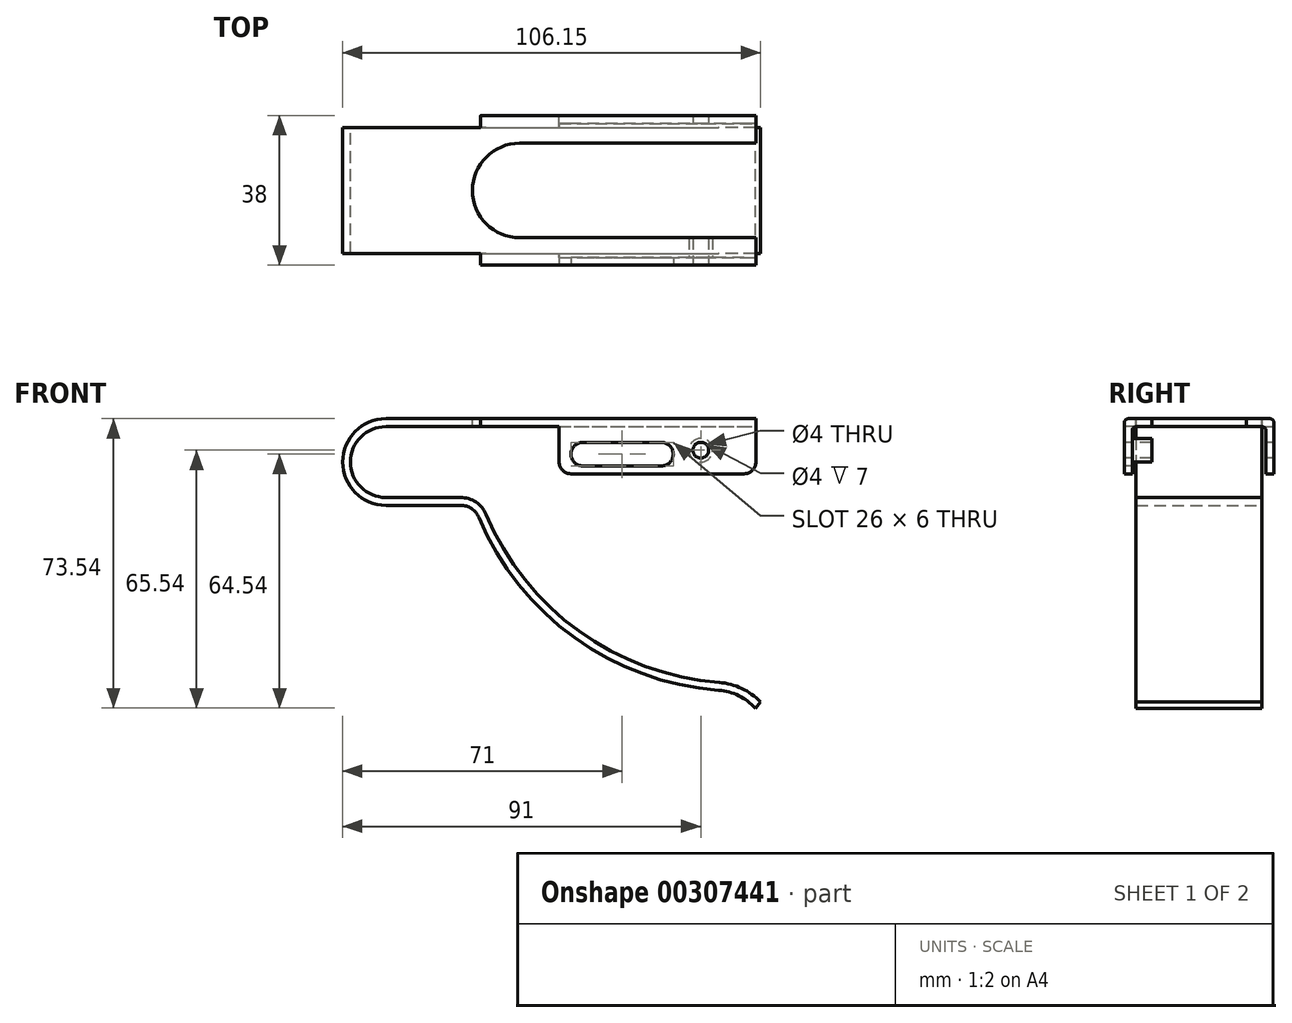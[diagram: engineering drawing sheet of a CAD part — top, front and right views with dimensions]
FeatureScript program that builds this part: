
annotation { "Feature Type Name" : "Feature", "Feature Type Description" : "" }
export const myFeature = defineFeature(function(context is Context, id is Id, definition is map)
    precondition{}
    {
        {
            var Q0;
            Q0=qCreatedBy(makeId("Front.planeOp"),FACE);
            var sketch = newSketch(context, id + "F0", { "sketchPlane" : qUnion([Q0])});
            skArc(sketch, "E0", {"start": v(0, 11) * mm, "mid": v(-11, 0) * mm, "end": v(0, -11) * mm});
            skLineSegment(sketch, "E1", {"start": v(0, 11) * mm, "end": v(94, 11) * mm});
            skLineSegment(sketch, "E2", {"start": v(0, -11) * mm, "end": v(19, -11) * mm});
            skArc(sketch, "E3", {"start": v(23.61, -14.06) * mm, "mid": v(47.9, -44.6) * mm, "end": v(84.55, -58) * mm});
            skArc(sketch, "E4", {"start": v(93.86, -62.54) * mm, "mid": v(89.64, -59.38) * mm, "end": v(84.55, -58) * mm});
            skPoint(sketch, "E5.visualSharp", {"position": v(22.4, -11) * mm});
            skArc(sketch, "E5.filletArc", {"start": v(23.61, -14.06) * mm, "mid": v(21.77, -11.84) * mm, "end": v(19, -11) * mm});
            skLineSegment(sketch, "E6.0", {"start": v(0, 9) * mm, "end": v(94, 9) * mm});
            skArc(sketch, "E6.1", {"start": v(0, 9) * mm, "mid": v(-9, 0) * mm, "end": v(0, -9) * mm});
            skArc(sketch, "E6.2", {"start": v(95.15, -61) * mm, "mid": v(90.4, -57.52) * mm, "end": v(84.7, -56) * mm});
            skArc(sketch, "E6.3", {"start": v(25.45, -13.3) * mm, "mid": v(49.07, -42.99) * mm, "end": v(84.7, -56) * mm});
            skArc(sketch, "E6.4", {"start": v(25.45, -13.3) * mm, "mid": v(22.88, -10.17) * mm, "end": v(19, -9) * mm});
            skLineSegment(sketch, "E6.5", {"start": v(0, -9) * mm, "end": v(19, -9) * mm});
            skLineSegment(sketch, "E7", {"start": v(94, 11) * mm, "end": v(94, 9) * mm});
            skLineSegment(sketch, "E8", {"start": v(95.15, -61) * mm, "end": v(93.86, -62.54) * mm});
            skLineSegment(sketch, "E9", {"start": v(107.63, -61.05) * mm, "end": v(113.07, -61.05) * mm});
            skSolve(sketch);
        }
        {
            var Q0;
            Q0 = qSketchRegion(id + "F0", true);
            extrude(context, id + "F1", {"entities" : qUnion([Q0]), "depth" : 16 * mm});
        }
        {
            var Q0;
            Q0=makeQuery(id+"F1.opExtrude","SWEPT_FACE",FACE,{"disambiguationData":[OSD([sQuery(id+"F0.wireOp",EDGE,"E1")])]});
            var sketch = newSketch(context, id + "F2", { "sketchPlane" : qUnion([Q0])});
            skLineSegment(sketch, "E10.bottom", {"start": v(94, -16) * mm, "end": v(24, -16) * mm});
            skLineSegment(sketch, "E10.top", {"start": v(94, -19) * mm, "end": v(24, -19) * mm});
            skLineSegment(sketch, "E10.left", {"start": v(94, -16) * mm, "end": v(94, -19) * mm});
            skLineSegment(sketch, "E10.right", {"start": v(24, -16) * mm, "end": v(24, -19) * mm});
            skSolve(sketch);
        }
        {
            var Q0;
            Q0 = qSketchRegion(id + "F2", true);
            extrude(context, id + "F3", {"entities" : qUnion([Q0]), "operationType" : NewBodyOperationType.ADD, "oppositeDirection" : true, "depth" : 2 * mm});
        }
        {
            var Q0;
            Q0=makeQuery(id+"F3.opExtrude","SWEPT_FACE",FACE,{"disambiguationData":[OSD([sQuery(id+"F2.wireOp",EDGE,"E10.top")])]});
            var sketch = newSketch(context, id + "F4", { "sketchPlane" : qUnion([Q0])});
            skLineSegment(sketch, "E11.bottom", {"start": v(94, 11) * mm, "end": v(44, 11) * mm});
            skLineSegment(sketch, "E11.top", {"start": v(94, -3) * mm, "end": v(44, -3) * mm});
            skLineSegment(sketch, "E11.left", {"start": v(94, 11) * mm, "end": v(94, -3) * mm});
            skLineSegment(sketch, "E11.right", {"start": v(44, 11) * mm, "end": v(44, -3) * mm});
            skSolve(sketch);
        }
        {
            var Q0;
            Q0 = qSketchRegion(id + "F4", true);
            extrude(context, id + "F5", {"entities" : qUnion([Q0]), "operationType" : NewBodyOperationType.ADD, "oppositeDirection" : true, "depth" : 2 * mm});
        }
        {
            var Q0;
            Q0=makeQuery(id+"F3.opExtrude","CAP_EDGE",EDGE,{"disambiguationData":[OSD([sQuery(id+"F2.wireOp",EDGE,"E10.top")])],"isStart":true});
            var Q1;
            Q1=makeQuery(id+"F5.boolean.opBoolean","INTERSECT",EDGE,{"derivedFrom":[makeQuery(id+"F3.boolean.opBoolean","MERGE",FACE,{"derivedFrom":[makeQuery(id+"F1.opExtrude","SWEPT_FACE",FACE,{"disambiguationData":[OSD([sQuery(id+"F0.wireOp",EDGE,"E6.0")])]}),makeQuery(id+"F3.opExtrude","CAP_FACE",FACE,{"disambiguationData":[OSD([sQuery(id+"F2.wireOp",EDGE,"E10.bottom"),sQuery(id+"F2.wireOp",EDGE,"E10.top"),sQuery(id+"F2.wireOp",EDGE,"E10.left"),sQuery(id+"F2.wireOp",EDGE,"E10.right")])],"isStart":false})]}),makeQuery(id+"F5.opExtrude","CAP_FACE",FACE,{"disambiguationData":[OSD([sQuery(id+"F4.wireOp",EDGE,"E11.bottom"),sQuery(id+"F4.wireOp",EDGE,"E11.top"),sQuery(id+"F4.wireOp",EDGE,"E11.left"),sQuery(id+"F4.wireOp",EDGE,"E11.right")])],"isStart":false})]});
            fillet(context, id + "F6", {"entities" : qUnion([Q0, Q1]), "radius" : 1 * mm, "tangentPropagation" : true, "allowEdgeOverflow" : false});
        }
        {
            var Q0;
            Q0=makeQuery(id+"F1.opExtrude","SWEPT_BODY",BODY,{"disambiguationData":[OSD([sQuery(id+"F0.wireOp",EDGE,"E0"),sQuery(id+"F0.wireOp",EDGE,"E1"),sQuery(id+"F0.wireOp",EDGE,"E2"),sQuery(id+"F0.wireOp",EDGE,"E3"),sQuery(id+"F0.wireOp",EDGE,"E4"),sQuery(id+"F0.wireOp",EDGE,"E5.filletArc"),sQuery(id+"F0.wireOp",EDGE,"E6.0"),sQuery(id+"F0.wireOp",EDGE,"E6.1"),sQuery(id+"F0.wireOp",EDGE,"E6.2"),sQuery(id+"F0.wireOp",EDGE,"E6.3"),sQuery(id+"F0.wireOp",EDGE,"E6.4"),sQuery(id+"F0.wireOp",EDGE,"E6.5"),sQuery(id+"F0.wireOp",EDGE,"E7"),sQuery(id+"F0.wireOp",EDGE,"E8")])]});
            var Q1;
            Q1=qCreatedBy(makeId("Front.planeOp"),FACE);
            mirror(context, id + "F7", {"operationType" : NewBodyOperationType.ADD, "entities" : qUnion([Q0]), "mirrorPlane" : qUnion([Q1])});
        }
        {
            var Q0;
            {var subQ0=makeQuery(id+"F3.boolean.opBoolean","MERGE",FACE,{"derivedFrom":[makeQuery(id+"F1.opExtrude","SWEPT_FACE",FACE,{"disambiguationData":[OSD([sQuery(id+"F0.wireOp",EDGE,"E1")])]}),makeQuery(id+"F3.opExtrude","CAP_FACE",FACE,{"disambiguationData":[OSD([sQuery(id+"F2.wireOp",EDGE,"E10.bottom"),sQuery(id+"F2.wireOp",EDGE,"E10.top"),sQuery(id+"F2.wireOp",EDGE,"E10.left"),sQuery(id+"F2.wireOp",EDGE,"E10.right")])],"isStart":true})]});Q0=makeQuery(id+"F7.boolean.opBoolean","MERGE",FACE,{"derivedFrom":[subQ0,makeQuery(id+"F7.opPattern","COPY",FACE,{"derivedFrom":subQ0,"instanceName":"1"})]});}
            var sketch = newSketch(context, id + "F8", { "sketchPlane" : qUnion([Q0])});
            skArc(sketch, "E12", {"start": v(34, 12) * mm, "mid": v(22, 0) * mm, "end": v(34, -12) * mm});
            skLineSegment(sketch, "E13", {"start": v(34, -12) * mm, "end": v(94, -12) * mm});
            skLineSegment(sketch, "E14", {"start": v(34, 12) * mm, "end": v(94, 12) * mm});
            skSolve(sketch);
        }
        {
            var Q0;
            Q0=makeQuery(id+"F8.imprint","IMPRINT",FACE,{"disambiguationData":[TD([[makeQuery(id+"F8.imprint","IMPRINT",EDGE,{"derivedFrom":sQuery(id+"F8.wireOp",EDGE,"E12")}),1.0]])]});
            extrude(context, id + "F9", {"entities" : qUnion([Q0]), "operationType" : NewBodyOperationType.REMOVE, "oppositeDirection" : true, "depth" : 2 * mm});
        }
        {
            var Q0;
            Q0=makeQuery(id+"F5.boolean.opBoolean","MERGE",FACE,{"derivedFrom":[makeQuery(id+"F3.opExtrude","SWEPT_FACE",FACE,{"disambiguationData":[OSD([sQuery(id+"F2.wireOp",EDGE,"E10.top")])]}),makeQuery(id+"F5.opExtrude","CAP_FACE",FACE,{"disambiguationData":[OSD([sQuery(id+"F4.wireOp",EDGE,"E11.bottom"),sQuery(id+"F4.wireOp",EDGE,"E11.top"),sQuery(id+"F4.wireOp",EDGE,"E11.left"),sQuery(id+"F4.wireOp",EDGE,"E11.right")])],"isStart":true})]});
            var sketch = newSketch(context, id + "F10", { "sketchPlane" : qUnion([Q0])});
            skLineSegment(sketch, "E15", {"start": v(50, 2) * mm, "end": v(70, 2) * mm});
            skArc(sketch, "E16.0.startCap", {"start": v(50, -1) * mm, "mid": v(47, 2) * mm, "end": v(50, 5) * mm});
            skArc(sketch, "E16.0.endCap", {"start": v(70, 5) * mm, "mid": v(73, 2) * mm, "end": v(70, -1) * mm});
            skLineSegment(sketch, "E16.0.left", {"start": v(50, 5) * mm, "end": v(70, 5) * mm});
            skLineSegment(sketch, "E16.0.right", {"start": v(50, -1) * mm, "end": v(70, -1) * mm});
            skSolve(sketch);
        }
        {
            var Q0;
            Q0 = qSketchRegion(id + "F10", true);
            extrude(context, id + "F11", {"entities" : qUnion([Q0]), "operationType" : NewBodyOperationType.REMOVE, "oppositeDirection" : true, "depth" : 25 * mm});
        }
        {
            var Q0;
            Q0=makeQuery(id+"F5.boolean.opBoolean","MERGE",FACE,{"derivedFrom":[makeQuery(id+"F3.opExtrude","SWEPT_FACE",FACE,{"disambiguationData":[OSD([sQuery(id+"F2.wireOp",EDGE,"E10.top")])]}),makeQuery(id+"F5.opExtrude","CAP_FACE",FACE,{"disambiguationData":[OSD([sQuery(id+"F4.wireOp",EDGE,"E11.bottom"),sQuery(id+"F4.wireOp",EDGE,"E11.top"),sQuery(id+"F4.wireOp",EDGE,"E11.left"),sQuery(id+"F4.wireOp",EDGE,"E11.right")])],"isStart":true})]});
            var sketch = newSketch(context, id + "F12", { "sketchPlane" : qUnion([Q0])});
            skPoint(sketch, "E17", {"position": v(80, 3) * mm});
            skSolve(sketch);
        }
        {
            var Q0;
            Q0=sQuery(id+"F12.wireOp",VERTEX,"E17");
            var Q1;
            Q1=makeQuery(id+"F1.opExtrude","SWEPT_BODY",BODY,{"disambiguationData":[OSD([sQuery(id+"F0.wireOp",EDGE,"E0"),sQuery(id+"F0.wireOp",EDGE,"E1"),sQuery(id+"F0.wireOp",EDGE,"E2"),sQuery(id+"F0.wireOp",EDGE,"E3"),sQuery(id+"F0.wireOp",EDGE,"E4"),sQuery(id+"F0.wireOp",EDGE,"E5.filletArc"),sQuery(id+"F0.wireOp",EDGE,"E6.0"),sQuery(id+"F0.wireOp",EDGE,"E6.1"),sQuery(id+"F0.wireOp",EDGE,"E6.2"),sQuery(id+"F0.wireOp",EDGE,"E6.3"),sQuery(id+"F0.wireOp",EDGE,"E6.4"),sQuery(id+"F0.wireOp",EDGE,"E6.5"),sQuery(id+"F0.wireOp",EDGE,"E7"),sQuery(id+"F0.wireOp",EDGE,"E8")])]});
            hole(context, id + "F13", {"style" : HoleStyle.SIMPLE, "endStyle" : HoleEndStyle.BLIND, "holeDiameter" : 4 * mm, "holeDepth" : 50 * mm, "isTappedThrough" : true, "tappedDepth" : 12 * mm, "tapClearance" : 3, "locations" : qUnion([Q0]), "scope" : qUnion([Q1])});
        }
        {
            var Q0;
            Q0=makeQuery(id+"F5.opExtrude","CAP_FACE",FACE,{"disambiguationData":[OSD([sQuery(id+"F4.wireOp",EDGE,"E11.bottom"),sQuery(id+"F4.wireOp",EDGE,"E11.top"),sQuery(id+"F4.wireOp",EDGE,"E11.left"),sQuery(id+"F4.wireOp",EDGE,"E11.right")])],"isStart":false});
            var sketch = newSketch(context, id + "F14", { "sketchPlane" : qUnion([Q0])});
            skCircle(sketch, "E18.0", {"center": v(-80, 3) * mm, "radius": 2 * mm});
            skCircle(sketch, "E19.0", {"center": v(-80, 3) * mm, "radius": 3 * mm});
            skSolve(sketch);
        }
        {
            var Q0;
            Q0 = qSketchRegion(id + "F14", true);
            extrude(context, id + "F15", {"entities" : qUnion([Q0]), "operationType" : NewBodyOperationType.ADD, "depth" : 5 * mm});
        }
        {
            var Q0;
            Q0=makeQuery(id+"F5.opExtrude","SWEPT_EDGE",EDGE,{"disambiguationData":[OSD([sQuery(id+"F4.wireOp",EDGE,"E11.top"),sQuery(id+"F4.wireOp",EDGE,"E11.left")])]});
            var Q1;
            Q1=makeQuery(id+"F7.opPattern","COPY",EDGE,{"derivedFrom":makeQuery(id+"F5.opExtrude","SWEPT_EDGE",EDGE,{"disambiguationData":[OSD([sQuery(id+"F4.wireOp",EDGE,"E11.top"),sQuery(id+"F4.wireOp",EDGE,"E11.left")])]}),"instanceName":"1"});
            var Q2;
            Q2=makeQuery(id+"F5.opExtrude","SWEPT_EDGE",EDGE,{"disambiguationData":[OSD([sQuery(id+"F4.wireOp",EDGE,"E11.top"),sQuery(id+"F4.wireOp",EDGE,"E11.right")])]});
            var Q3;
            Q3=makeQuery(id+"F7.opPattern","COPY",EDGE,{"derivedFrom":makeQuery(id+"F5.opExtrude","SWEPT_EDGE",EDGE,{"disambiguationData":[OSD([sQuery(id+"F4.wireOp",EDGE,"E11.top"),sQuery(id+"F4.wireOp",EDGE,"E11.right")])]}),"instanceName":"1"});
            fillet(context, id + "F16", {"entities" : qUnion([Q0, Q1, Q2, Q3]), "radius" : 3 * mm, "tangentPropagation" : true, "allowEdgeOverflow" : false});
        }
    });
